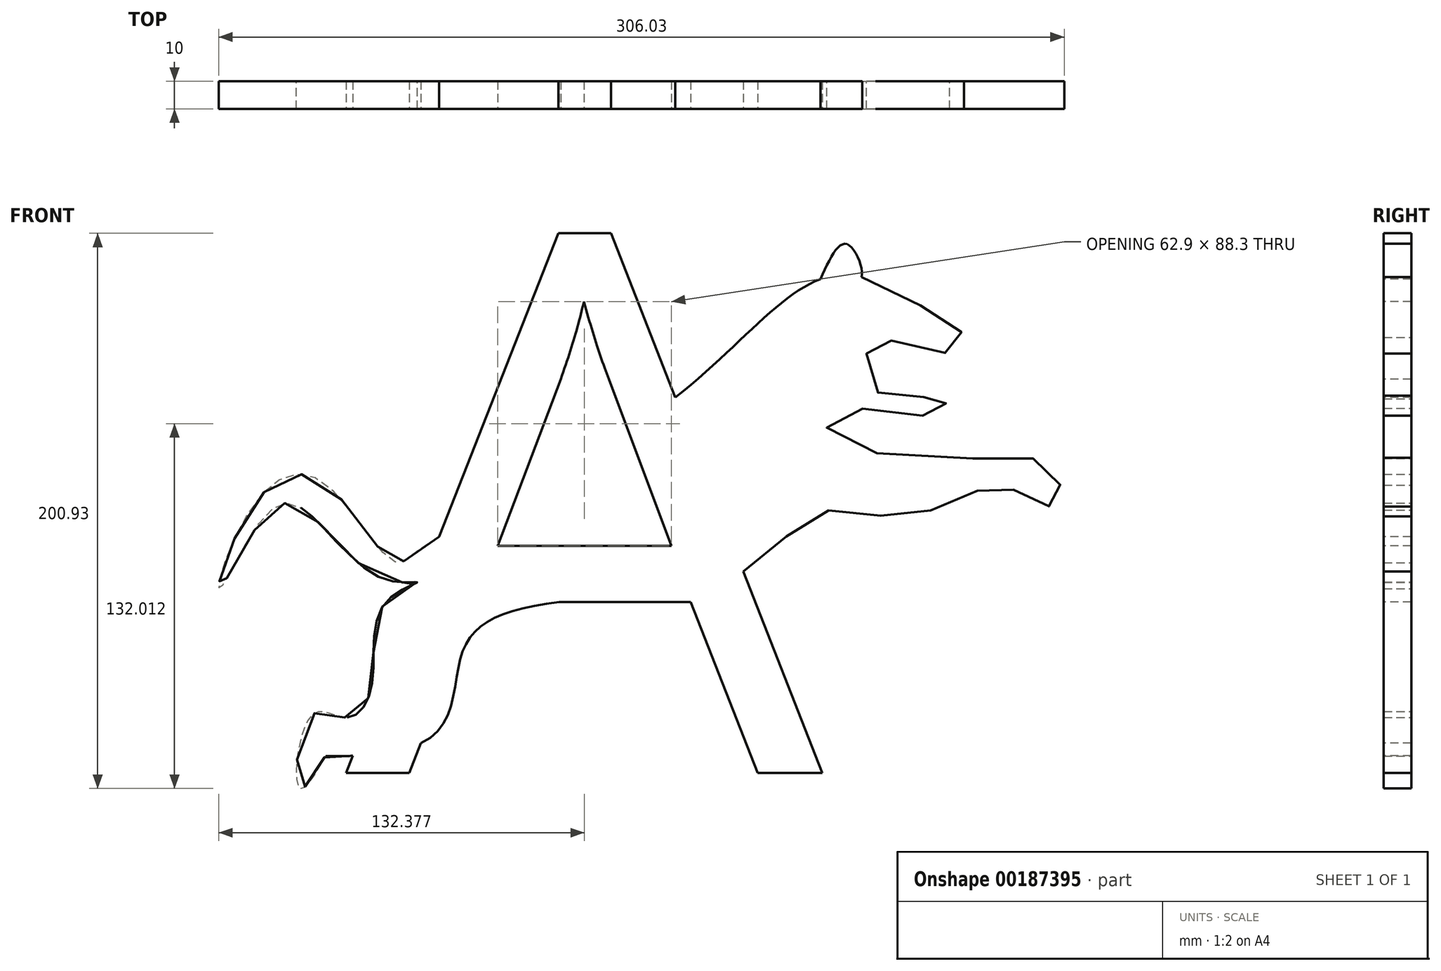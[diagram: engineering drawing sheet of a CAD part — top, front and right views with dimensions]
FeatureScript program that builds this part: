
annotation { "Feature Type Name" : "Feature", "Feature Type Description" : "" }
export const myFeature = defineFeature(function(context is Context, id is Id, definition is map)
    precondition{}
    {
        {
            var Q0;
            Q0=qCreatedBy(makeId("Front.planeOp"),FACE);
            var sketch = newSketch(context, id + "F0", { "sketchPlane" : qUnion([Q0])});
            skText(sketch, "E0", { "text": "A", "fontName": "OpenSans-Regular.ttf"});
            skPoint(sketch, "E1.23.internal.snap0", {"position": v(51.12, 85.76) * mm});
            skPoint(sketch, "E1.25.internal.snap0", {"position": v(51.12, 85.76) * mm});
            skPoint(sketch, "E1.26.internal.snap0", {"position": v(51.12, 85.76) * mm});
            skFitSpline(sketch, "E1", {"points": [v(-111.27, 69.28) * mm, v(-122.06, 64.33) * mm, v(-147.7, 93.1) * mm, v(-168.37, 89.5) * mm, v(-184.56, 58.04) * mm, v(-184.56, 54.44) * mm, v(-168.37, 80.52) * mm, v(-155.33, 83.66) * mm, v(-125.66, 58.04) * mm, v(-113.07, 56.69) * mm, v(-125.2, 48.6) * mm, v(-129.7, 18.92) * mm, v(-138.88, 7.68) * mm, v(-151.29, 8.58) * mm, v(-155.33, -17.95) * mm, v(-146.8, -6.71) * mm, v(-146.34, -6.26) * mm, v(-109.02, 0) * mm, v(-97.33, 29.7) * mm, v(-81.15, 45.45) * mm, v(-22.7, 53.54) * mm, v(11.48, 64.78) * mm, v(32.16, 81.87) * mm, v(57.34, 80.52) * mm, v(80.72, 85.76) * mm, v(98.7, 91.76) * mm, v(109.5, 85.76) * mm, v(120.73, 85.76) * mm, v(114.44, 98.95) * mm, v(101.4, 101.65) * mm, v(37.1, 108.84) * mm, v(38.9, 118.28) * mm, v(70.38, 116.94) * mm, v(75.77, 119.18) * mm, v(79.37, 123.68) * mm, v(58.24, 123.23) * mm, v(51.12, 130.42) * mm, v(51.12, 144.81) * mm, v(74.42, 139.42) * mm, v(84.76, 144.81) * mm, v(73.97, 153.8) * mm, v(38.45, 167.74) * mm, v(-21.35, 122.33) * mm, v(-111.27, 69.28) * mm]});
            skFitSpline(sketch, "E2", {"points": [v(32.77, 166.34) * mm, v(42.5, 178.98) * mm, v(47.62, 167.1) * mm, v(38.45, 167.74) * mm], "startDerivative": vector(25.3, 55.8) * mm, "endDerivative": vector(-43.02, 15.42) * mm});
            const initialGuessF0  = {"E0": [-0.13888, -0.01229, 1, 0, 0.19609]};
            skSetInitialGuess(sketch, initialGuessF0);
            skSolve(sketch);
        }
        {
            var Q0;
            Q0 = qSketchRegion(id + "F0", true);
            extrude(context, id + "F1", {"entities" : qUnion([Q0]), "oppositeDirection" : true, "depth" : 10 * mm});
        }
    });
